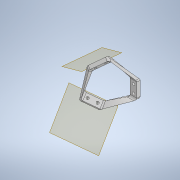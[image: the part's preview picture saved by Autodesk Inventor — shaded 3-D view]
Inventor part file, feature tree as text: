
AUTODESK INVENTOR PART (.ipt)
format: ipt  version: 2020 (Build 240168000, 168)  size: 510,464 bytes
history: native  units: mm
features: other x11, extrude x3, loft x3, fillet x3, sketch x3, reference x3, plane x2
ambient origin geometry x8: Origin, YZ Plane, XZ Plane, XY Plane, X Axis, Y Axis, Z Axis, Center Point
bodies: Solid1 (feature_tree)
feature tree (28):
  extrude  "Extrusion1"  Depth=3.0mm
  plane  "Work Plane1"
  extrude  "Extrusion2"  Depth=3.0mm
  plane  "Work Plane2"
  extrude  "Extrusion3"  Depth=4.0mm TaperAngle=0.0deg
  loft  "Loft1"
  loft  "Loft2"
  loft  "Loft3"
  fillet  "Fillet1"  [1 undecoded]
  fillet  "Fillet2"  [1 undecoded]
  fillet  "Fillet3"  [1 undecoded]
  sketch  "Sketch1"  dims[d0=3.0mm d1=3.0mm]
  reference  "Reference1"
  sketch  "Sketch2"  dims[d2=4.0mm d3=0.0mm d4=3.0mm]
  reference  "Reference2"
  sketch  "Sketch3"  dims[d5=3.0mm d6=4.0mm d7=0.0mm d8=3.0mm d9=3.0mm d10=4.0mm d11=0.0mm d12=0.0mm d13=90.0deg d14=0.0mm d15=90.0deg d16=0.0mm d17=90.0deg d18=0.0mm d19=90.0deg d20=0.0mm d21=90.0deg d22=0.0mm d23=90.0deg d24=3.0mm d25=3.0mm d26=3.0mm]
  reference  "Reference3"
  other  "Edges1"
  other  "Edges2"
  other  "Edges3"
  other  "Edges4"
  other  "Edges5"
  other  "Edges6"
  parser-record x1  (decoder bookkeeping rows leaked as tree rows — omitted from the tree; the rows remain in map.json)
  other  "delta_1.iam"
  other  "arm_holder_2:2"
  other  "arm_holder_2:3"
  other  "arm_holder_2:1"
note: 3 required parameter values undecoded (feature->parameter linkage not recoverable at this tier; creation-order binding heuristic only, values carry confidence <= 0.55)
note: 1 file-system path scrubbed to <path> (originals preserved in map.json)
